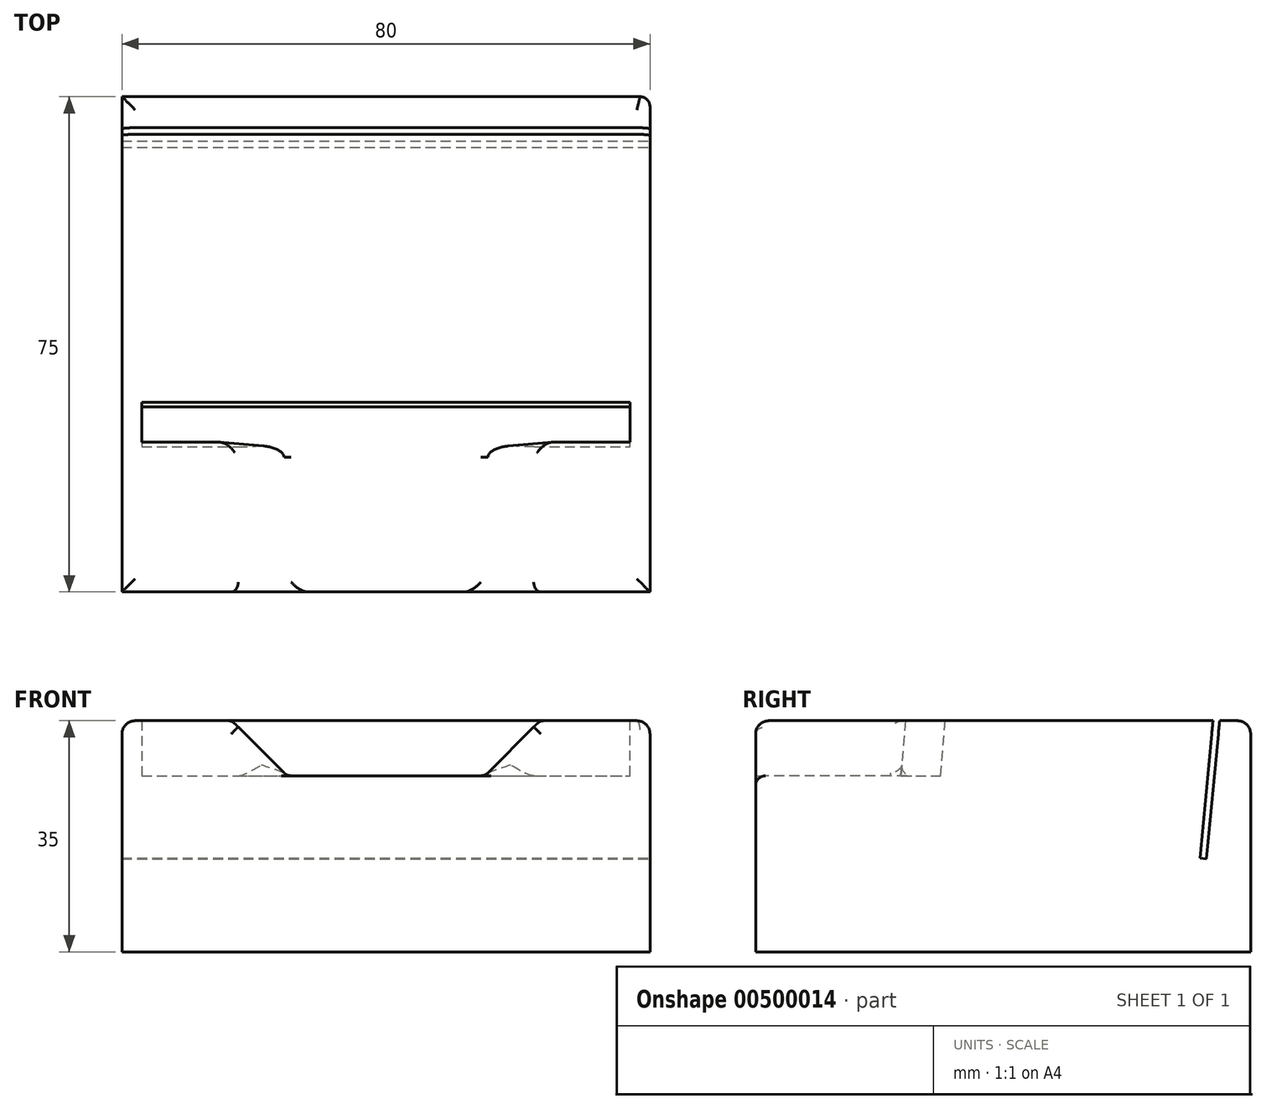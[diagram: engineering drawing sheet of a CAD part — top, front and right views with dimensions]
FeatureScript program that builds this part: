
annotation { "Feature Type Name" : "Feature", "Feature Type Description" : "" }
export const myFeature = defineFeature(function(context is Context, id is Id, definition is map)
    precondition{}
    {
        {
            var Q0;
            Q0=qCreatedBy(makeId("Right.planeOp"),FACE);
            var sketch = newSketch(context, id + "F0", { "sketchPlane" : qUnion([Q0])});
            skLineSegment(sketch, "E0.bottom", {"start": v(0, 0) * mm, "end": v(75, 0) * mm});
            skLineSegment(sketch, "E0.top", {"start": v(0, 25) * mm, "end": v(75, 25) * mm});
            skLineSegment(sketch, "E0.left", {"start": v(0, 0) * mm, "end": v(0, 25) * mm});
            skLineSegment(sketch, "E0.right", {"start": v(75, 0) * mm, "end": v(75, 25) * mm});
            skSolve(sketch);
        }
        {
            var Q0;
            Q0 = qSketchRegion(id + "F0", true);
            extrude(context, id + "F1", {"entities" : qUnion([Q0]), "depth" : 80 * mm});
        }
        {
            var Q0;
            Q0=makeQuery(id+"F1.opExtrude","CAP_FACE",FACE,{"disambiguationData":[OSD([sQuery(id+"F0.wireOp",EDGE,"E0.bottom"),sQuery(id+"F0.wireOp",EDGE,"E0.top"),sQuery(id+"F0.wireOp",EDGE,"E0.left"),sQuery(id+"F0.wireOp",EDGE,"E0.right")])],"isStart":false});
            var sketch = newSketch(context, id + "F2", { "sketchPlane" : qUnion([Q0])});
            skLineSegment(sketch, "E1", {"start": v(22.72, 25) * mm, "end": v(21.99, 16.67) * mm});
            skLineSegment(sketch, "E2", {"start": v(21.99, 16.67) * mm, "end": v(28.01, 16.67) * mm});
            skLineSegment(sketch, "E3", {"start": v(28.01, 16.67) * mm, "end": v(28.74, 25) * mm});
            skPoint(sketch, "E4", {"position": v(25, 16.67) * mm});
            skLineSegment(sketch, "E5", {"start": v(69.3, 25) * mm, "end": v(67.32, 4.18) * mm});
            skLineSegment(sketch, "E6", {"start": v(67.32, 4.18) * mm, "end": v(68.31, 4.09) * mm});
            skLineSegment(sketch, "E7", {"start": v(68.31, 4.09) * mm, "end": v(70.3, 25) * mm});
            skLineSegment(sketch, "E8", {"start": v(70.3, 25) * mm, "end": v(69.3, 25) * mm});
            skSolve(sketch);
        }
        {
            var Q0;
            {var subQ0=sQuery(id+"F2.wireOp",EDGE,"E1");Q0=makeQuery(id+"F2.imprint","IMPRINT",FACE,{"disambiguationData":[TD([[makeQuery(id+"F2.imprint","IMPRINT",EDGE,{"derivedFrom":subQ0}),1.0]])]});}
            var Q1;
            Q1=makeQuery(id+"F2.imprint","IMPRINT",FACE,{"disambiguationData":[TD([[makeQuery(id+"F2.imprint","IMPRINT",EDGE,{"derivedFrom":sQuery(id+"F2.wireOp",EDGE,"E5")}),1.0]])]});
            extrude(context, id + "F3", {"entities" : qUnion([Q0, Q1]), "operationType" : NewBodyOperationType.REMOVE, "oppositeDirection" : true, "depth" : 80 * mm, "offsetDistance" : 25 * mm});
        }
        {
            var Q0;
            Q0=makeQuery(id+"F1.opExtrude","SWEPT_FACE",FACE,{"disambiguationData":[OSD([sQuery(id+"F0.wireOp",EDGE,"E0.left")])]});
            var sketch = newSketch(context, id + "F4", { "sketchPlane" : qUnion([Q0])});
            skLineSegment(sketch, "E9", {"start": v(16.67, 25) * mm, "end": v(25, 16.67) * mm});
            skLineSegment(sketch, "E10", {"start": v(25, 16.67) * mm, "end": v(55, 16.67) * mm});
            skLineSegment(sketch, "E11", {"start": v(55, 16.67) * mm, "end": v(63.33, 25) * mm});
            skLineSegment(sketch, "E12", {"start": v(63.33, 25) * mm, "end": v(16.67, 25) * mm});
            skPoint(sketch, "E13", {"position": v(40, 16.67) * mm});
            skPoint(sketch, "E14", {"position": v(40, 0) * mm});
            skSolve(sketch);
        }
        {
            var Q0;
            Q0 = qSketchRegion(id + "F4", true);
            extrude(context, id + "F5", {"entities" : qUnion([Q0]), "operationType" : NewBodyOperationType.REMOVE, "oppositeDirection" : true, "depth" : 23.7 * mm});
        }
        {
            var Q0;
            Q0=makeQuery(id+"F1.opExtrude","CAP_FACE",FACE,{"disambiguationData":[OSD([sQuery(id+"F0.wireOp",EDGE,"E0.bottom"),sQuery(id+"F0.wireOp",EDGE,"E0.top"),sQuery(id+"F0.wireOp",EDGE,"E0.left"),sQuery(id+"F0.wireOp",EDGE,"E0.right")])],"isStart":false});
            var sketch = newSketch(context, id + "F6", { "sketchPlane" : qUnion([Q0])});
            skLineSegment(sketch, "E15", {"start": v(28.74, 25) * mm, "end": v(22.72, 25) * mm});
            skLineSegment(sketch, "E16", {"start": v(22.72, 25) * mm, "end": v(21.99, 16.67) * mm});
            skLineSegment(sketch, "E17", {"start": v(21.99, 16.67) * mm, "end": v(28.01, 16.67) * mm});
            skLineSegment(sketch, "E18", {"start": v(28.01, 16.67) * mm, "end": v(28.74, 25) * mm});
            skSolve(sketch);
        }
        {
            var Q0;
            Q0 = qSketchRegion(id + "F6", true);
            extrude(context, id + "F7", {"entities" : qUnion([Q0]), "operationType" : NewBodyOperationType.ADD, "oppositeDirection" : true, "depth" : 3 * mm, "offsetDistance" : 25 * mm});
        }
        {
            var Q0;
            Q0 = qSketchRegion(id + "F6", true);
            extrude(context, id + "F8", {"entities" : qUnion([Q0]), "operationType" : NewBodyOperationType.ADD, "oppositeDirection" : true, "depth" : 80 * mm, "offsetDistance" : 25 * mm, "hasSecondDirection" : true, "secondDirectionOppositeDirection" : true, "secondDirectionDepth" : 77 * mm});
        }
        {
            var Q0;
            {var subQ0=sQuery(id+"F0.wireOp",EDGE,"E0.right");var subQ1=sQuery(id+"F0.wireOp",EDGE,"E0.top");Q0=makeQuery(id+"F3.boolean.opBoolean","SPLIT",EDGE,{"disambiguationData":[TD([makeQuery(id+"F1.opExtrude","SWEPT_FACE",FACE,{"disambiguationData":[OSD([subQ0])]})])],"derivedFrom":makeQuery(id+"F1.opExtrude","CAP_EDGE",EDGE,{"disambiguationData":[OSD([subQ1])],"isStart":false})});}
            var Q1;
            Q1=makeQuery(id+"F1.opExtrude","SWEPT_EDGE",EDGE,{"disambiguationData":[OSD([sQuery(id+"F0.wireOp",EDGE,"E0.top"),sQuery(id+"F0.wireOp",EDGE,"E0.right")])]});
            var Q2;
            {var subQ0=sQuery(id+"F0.wireOp",EDGE,"E0.right");var subQ1=sQuery(id+"F0.wireOp",EDGE,"E0.top");Q2=makeQuery(id+"F3.boolean.opBoolean","SPLIT",EDGE,{"disambiguationData":[TD([makeQuery(id+"F1.opExtrude","SWEPT_FACE",FACE,{"disambiguationData":[OSD([subQ0])]})])],"derivedFrom":makeQuery(id+"F1.opExtrude","CAP_EDGE",EDGE,{"disambiguationData":[OSD([subQ1])],"isStart":true})});}
            var Q3;
            {var subQ0=sQuery(id+"F0.wireOp",EDGE,"E0.left");var subQ1=sQuery(id+"F0.wireOp",EDGE,"E0.top");Q3=makeQuery(id+"F3.boolean.opBoolean","SPLIT",EDGE,{"disambiguationData":[TD([makeQuery(id+"F1.opExtrude","SWEPT_FACE",FACE,{"disambiguationData":[OSD([subQ0])]})])],"derivedFrom":makeQuery(id+"F1.opExtrude","CAP_EDGE",EDGE,{"disambiguationData":[OSD([subQ1])],"isStart":true})});}
            var Q4;
            {var subQ0=sQuery(id+"F0.wireOp",EDGE,"E0.left");var subQ1=sQuery(id+"F0.wireOp",EDGE,"E0.top");Q4=makeQuery(id+"F5.boolean.opBoolean","SPLIT",EDGE,{"disambiguationData":[TD([makeQuery(id+"F5.opExtrude","SWEPT_FACE",FACE,{"disambiguationData":[OSD([sQuery(id+"F4.wireOp",EDGE,"E9")])]})])],"derivedFrom":makeQuery(id+"F1.opExtrude","SWEPT_EDGE",EDGE,{"disambiguationData":[OSD([subQ1,subQ0])]})});}
            var Q5;
            {var subQ0=sQuery(id+"F0.wireOp",EDGE,"E0.left");var subQ1=sQuery(id+"F0.wireOp",EDGE,"E0.top");Q5=makeQuery(id+"F5.boolean.opBoolean","SPLIT",EDGE,{"disambiguationData":[TD([makeQuery(id+"F5.opExtrude","SWEPT_FACE",FACE,{"disambiguationData":[OSD([sQuery(id+"F4.wireOp",EDGE,"E11")])]})])],"derivedFrom":makeQuery(id+"F1.opExtrude","SWEPT_EDGE",EDGE,{"disambiguationData":[OSD([subQ1,subQ0])]})});}
            var Q6;
            {var subQ0=sQuery(id+"F0.wireOp",EDGE,"E0.left");var subQ1=sQuery(id+"F0.wireOp",EDGE,"E0.top");Q6=makeQuery(id+"F3.boolean.opBoolean","SPLIT",EDGE,{"disambiguationData":[TD([makeQuery(id+"F1.opExtrude","SWEPT_FACE",FACE,{"disambiguationData":[OSD([subQ0])]})])],"derivedFrom":makeQuery(id+"F1.opExtrude","CAP_EDGE",EDGE,{"disambiguationData":[OSD([subQ1])],"isStart":false})});}
            var Q7;
            {var subQ0=sQuery(id+"F0.wireOp",EDGE,"E0.top");Q7=makeQuery(id+"F3.boolean.opBoolean","SPLIT",EDGE,{"disambiguationData":[TD([makeQuery(id+"F3.opExtrude","SWEPT_FACE",FACE,{"disambiguationData":[OSD([sQuery(id+"F2.wireOp",EDGE,"E3")])]})])],"derivedFrom":makeQuery(id+"F1.opExtrude","CAP_EDGE",EDGE,{"disambiguationData":[OSD([subQ0])],"isStart":false})});}
            var Q8;
            {var subQ0=sQuery(id+"F0.wireOp",EDGE,"E0.top");Q8=makeQuery(id+"F3.boolean.opBoolean","SPLIT",EDGE,{"disambiguationData":[TD([makeQuery(id+"F3.opExtrude","SWEPT_FACE",FACE,{"disambiguationData":[OSD([sQuery(id+"F2.wireOp",EDGE,"E3")])]})])],"derivedFrom":makeQuery(id+"F1.opExtrude","CAP_EDGE",EDGE,{"disambiguationData":[OSD([subQ0])],"isStart":true})});}
            fillet(context, id + "F9", {"entities" : qUnion([Q0, Q1, Q2, Q3, Q4, Q5, Q6, Q7, Q8]), "radius" : 2 * mm, "tangentPropagation" : true, "allowEdgeOverflow" : false});
        }
        {
            var Q0;
            {var subQ0=sQuery(id+"F0.wireOp",EDGE,"E0.right");var subQ1=sQuery(id+"F0.wireOp",EDGE,"E0.top");Q0=makeQuery(id+"F9.opFillet","BLEND_EDGE",EDGE,{"blendedFrom":[makeQuery(id+"F1.opExtrude","SWEPT_EDGE",EDGE,{"disambiguationData":[OSD([subQ1,subQ0])]}),makeQuery(id+"F3.boolean.opBoolean","SPLIT",EDGE,{"disambiguationData":[TD([makeQuery(id+"F1.opExtrude","SWEPT_FACE",FACE,{"disambiguationData":[OSD([subQ0])]})])],"derivedFrom":makeQuery(id+"F1.opExtrude","CAP_EDGE",EDGE,{"disambiguationData":[OSD([subQ1])],"isStart":false})})],"blendedInto":[]});}
            var Q1;
            {var subQ0=sQuery(id+"F0.wireOp",EDGE,"E0.right");var subQ2=sQuery(id+"F0.wireOp",EDGE,"E0.top");Q1=makeQuery(id+"F9.opFillet","BLEND_EDGE",EDGE,{"blendedFrom":[makeQuery(id+"F1.opExtrude","SWEPT_EDGE",EDGE,{"disambiguationData":[OSD([subQ2,subQ0])]}),makeQuery(id+"F3.boolean.opBoolean","SPLIT",FACE,{"disambiguationData":[TD([makeQuery(id+"F1.opExtrude","SWEPT_FACE",FACE,{"disambiguationData":[OSD([subQ0])]})])],"derivedFrom":makeQuery(id+"F1.opExtrude","SWEPT_FACE",FACE,{"disambiguationData":[OSD([subQ2])]})})],"blendedInto":[makeQuery(id+"F3.boolean.opBoolean","SPLIT",FACE,{"disambiguationData":[TD([makeQuery(id+"F1.opExtrude","SWEPT_FACE",FACE,{"disambiguationData":[OSD([subQ0])]})])],"derivedFrom":makeQuery(id+"F1.opExtrude","SWEPT_FACE",FACE,{"disambiguationData":[OSD([subQ2])]})})]});}
            var Q2;
            {var subQ0=sQuery(id+"F0.wireOp",EDGE,"E0.right");Q2=makeQuery(id+"F9.opFillet","BLEND_EDGE",EDGE,{"blendedFrom":[makeQuery(id+"F1.opExtrude","SWEPT_EDGE",EDGE,{"disambiguationData":[OSD([sQuery(id+"F0.wireOp",EDGE,"E0.top"),subQ0])]}),makeQuery(id+"F1.opExtrude","SWEPT_FACE",FACE,{"disambiguationData":[OSD([subQ0])]})],"blendedInto":[makeQuery(id+"F1.opExtrude","SWEPT_FACE",FACE,{"disambiguationData":[OSD([subQ0])]})]});}
            var Q3;
            {var subQ0=sQuery(id+"F0.wireOp",EDGE,"E0.right");var subQ1=sQuery(id+"F0.wireOp",EDGE,"E0.top");var subQ2=makeQuery(id+"F1.opExtrude","CAP_FACE",FACE,{"disambiguationData":[OSD([sQuery(id+"F0.wireOp",EDGE,"E0.bottom"),subQ1,sQuery(id+"F0.wireOp",EDGE,"E0.left"),subQ0])],"isStart":false});Q3=makeQuery(id+"F9.opFillet","BLEND_EDGE",EDGE,{"blendedFrom":[makeQuery(id+"F3.boolean.opBoolean","SPLIT",EDGE,{"disambiguationData":[TD([makeQuery(id+"F1.opExtrude","SWEPT_FACE",FACE,{"disambiguationData":[OSD([subQ0])]})])],"derivedFrom":makeQuery(id+"F1.opExtrude","CAP_EDGE",EDGE,{"disambiguationData":[OSD([subQ1])],"isStart":false})}),subQ2],"blendedInto":[subQ2]});}
            var Q4;
            {var subQ0=sQuery(id+"F0.wireOp",EDGE,"E0.right");var subQ2=sQuery(id+"F0.wireOp",EDGE,"E0.top");var subQ5=makeQuery(id+"F1.opExtrude","SWEPT_FACE",FACE,{"disambiguationData":[OSD([subQ0])]});var subQ7=makeQuery(id+"F1.opExtrude","SWEPT_FACE",FACE,{"disambiguationData":[OSD([subQ2])]});Q4=makeQuery(id+"F9.opFillet","BLEND_EDGE",EDGE,{"blendedFrom":[makeQuery(id+"F3.boolean.opBoolean","SPLIT",EDGE,{"disambiguationData":[TD([subQ5])],"derivedFrom":makeQuery(id+"F1.opExtrude","CAP_EDGE",EDGE,{"disambiguationData":[OSD([subQ2])],"isStart":false})}),makeQuery(id+"F3.boolean.opBoolean","SPLIT",FACE,{"disambiguationData":[TD([subQ5])],"derivedFrom":subQ7})],"blendedInto":[makeQuery(id+"F3.boolean.opBoolean","SPLIT",FACE,{"disambiguationData":[TD([subQ5])],"derivedFrom":subQ7})]});}
            var Q5;
            Q5=makeQuery(id+"F5.boolean.opBoolean","COPY",FACE,{"derivedFrom":makeQuery(id+"F5.opExtrude","SWEPT_FACE",FACE,{"disambiguationData":[OSD([sQuery(id+"F4.wireOp",EDGE,"E9")])]})});
            var Q6;
            Q6=makeQuery(id+"F5.boolean.opBoolean","COPY",FACE,{"derivedFrom":makeQuery(id+"F5.opExtrude","SWEPT_FACE",FACE,{"disambiguationData":[OSD([sQuery(id+"F4.wireOp",EDGE,"E11")])]})});
            fillet(context, id + "F10", {"entities" : qUnion([Q0, Q1, Q2, Q3, Q4, Q5, Q6]), "radius" : 1.5 * mm, "tangentPropagation" : true, "allowEdgeOverflow" : false});
        }
        {
            var Q0;
            Q0=makeQuery(id+"F1.opExtrude","SWEPT_FACE",FACE,{"disambiguationData":[OSD([sQuery(id+"F0.wireOp",EDGE,"E0.bottom")])]});
            extrude(context, id + "F11", {"entities" : qUnion([Q0]), "operationType" : NewBodyOperationType.ADD, "depth" : 10 * mm, "offsetDistance" : 25 * mm});
        }
    });
